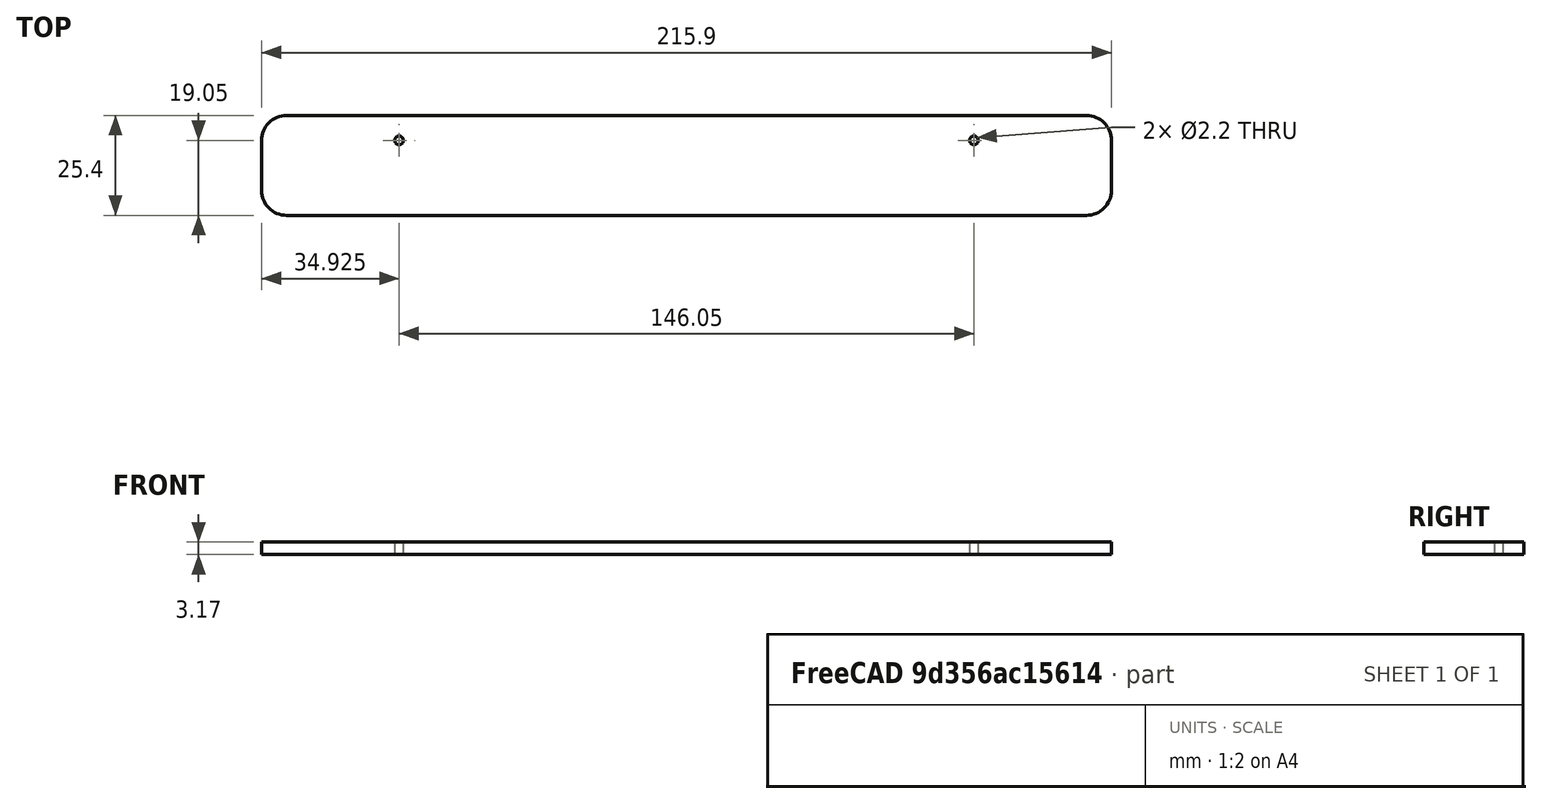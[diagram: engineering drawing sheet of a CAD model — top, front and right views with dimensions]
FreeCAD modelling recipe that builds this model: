
FCSTD DOCUMENT  (FreeCAD 0.19R23141 (Git))
Label: X23_Foot2
License: All rights reserved
LicenseURL: http://en.wikipedia.org/wiki/All_rights_reserved
objects: Sketcher::SketchObject×1, PartDesign::Pad×1, PartDesign::Body×1, PartDesign::CoordinateSystem×1, App::Part×1
note: 5 computed .brp shape members not serialized (recipe doc carries the construction recipe); baked Part::Feature solids carry a one-line shape summary decoded from their .brp

FEATURE [Sketcher::SketchObject] Sketch
  MapMode = 5
  Support = -> [XY_Plane]
  sketch-geometry (11):
    g0: LineSegment StartX=-101.6 StartY=12.7 StartZ=0 EndX=101.6 EndY=12.7 EndZ=0
    g1: LineSegment StartX=107.95 StartY=6.35 StartZ=0 EndX=107.95 EndY=-6.35 EndZ=0
    g2: LineSegment StartX=101.6 StartY=-12.7 StartZ=0 EndX=-101.6 EndY=-12.7 EndZ=0
    g3: LineSegment StartX=-107.95 StartY=-6.35 StartZ=0 EndX=-107.95 EndY=6.35 EndZ=0
    g4: ArcOfCircle CenterX=-101.6 CenterY=6.35 CenterZ=0 NormalX=0 NormalY=0 NormalZ=1 AngleXU=0 Radius=6.35 StartAngle=1.5708 EndAngle=3.14159
    g5: ArcOfCircle CenterX=-101.6 CenterY=-6.35 CenterZ=0 NormalX=0 NormalY=0 NormalZ=1 AngleXU=0 Radius=6.35 StartAngle=3.14159 EndAngle=4.71239
    g6: ArcOfCircle CenterX=101.6 CenterY=-6.35 CenterZ=0 NormalX=0 NormalY=0 NormalZ=1 AngleXU=0 Radius=6.35 StartAngle=4.71239 EndAngle=6.28319
    g7: ArcOfCircle CenterX=101.6 CenterY=6.35 CenterZ=0 NormalX=0 NormalY=0 NormalZ=1 AngleXU=0 Radius=6.35 StartAngle=0 EndAngle=1.5708
    g8: Circle CenterX=-73.025 CenterY=6.35 CenterZ=0 NormalX=0 NormalY=0 NormalZ=1 AngleXU=0 Radius=1.1
    g9: Circle CenterX=73.025 CenterY=6.35 CenterZ=0 NormalX=0 NormalY=0 NormalZ=1 AngleXU=0 Radius=1.1
    g10: LineSegment [constr] StartX=0 StartY=0 StartZ=0 EndX=0 EndY=6.35 EndZ=0
  constraints (27):
    c: Horizontal(g0)
    c: Horizontal(g2)
    c: Vertical(g1)
    c: Vertical(g3)
    c: Tangent(g0,g4) = 1.5708
    c: Tangent(g3,g4) = 1.5708
    c: Tangent(g2,g5) = 1.5708
    c: Tangent(g3,g5) = 1.5708
    c: Tangent(g2,g6) = 1.5708
    c: Tangent(g1,g6) = 1.5708
    c: Tangent(g1,g7) = 1.5708
    c: Tangent(g0,g7) = 1.5708
    c: DistanceX(g3,g1) = 215.9
    c: Equal(g4,g5)
    c: Equal(g5,g6)
    c: Equal(g6,g7)
    c: Radius(g4) = 6.35
    c: Symmetric(g4,g6,g-1)
    c: DistanceY(g2,g0) = 25.4
    c: Equal(g8,g9)
    c: DistanceX(g8,g9) = 146.05
    c: Diameter(g8) = 2.2
    c: Coincident(g10,g-1)
    c: Vertical(g10)
    c: Symmetric(g8,g9,g10)
    c: Horizontal(g10,g8)
    c: DistanceY(g10,g10) = 6.35
FEATURE [PartDesign::Pad] Pad
  Direction = (1,1,1)
  Length = 3.175
  Length2 = 99.9998
  Profile = -> Sketch
  Type = 0
FEATURE [PartDesign::Body] Body
  Group = -> [Sketch,Pad]
  Origin = -> Origin
  Tip = -> Pad
FEATURE [PartDesign::CoordinateSystem] LCS_0
  AttacherType = Attacher::AttachEngine3D
  MapMode = 2
  Support = -> [X_Axis001]
FEATURE [App::Part] Part
  Group = -> [LCS_0,Body]
  Origin = -> Origin001
